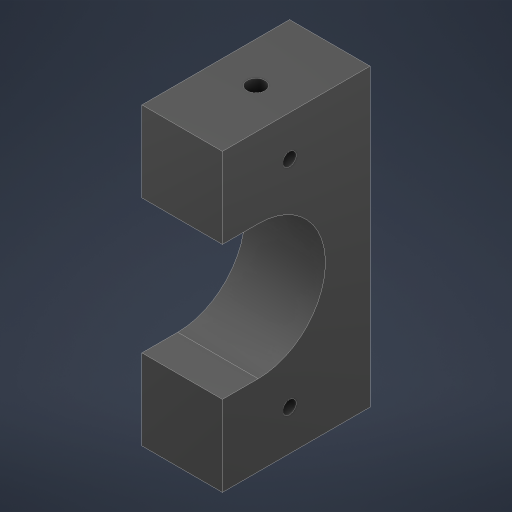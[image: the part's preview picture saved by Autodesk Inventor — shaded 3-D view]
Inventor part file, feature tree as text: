
AUTODESK INVENTOR PART (.ipt)
format: ipt  version: 2024 (Build 280153000, 153)  size: 223,232 bytes
history: native  units: in
note: dims shown in document units (in); Inventor stores cm internally (conversion verified against a paired STEP export)
features: extrude x2, sketch x2, other x1
ambient origin geometry x8: Origin, YZ Plane, XZ Plane, XY Plane, X Axis, Y Axis, Z Axis, Center Point
bodies: Body1 (feature_tree)
feature tree (5):
  other  "Sólido1"
  extrude  "Extrusión1"  Depth=0.3543in
  extrude  "Extrusión2"  Depth=0.1969in TaperAngle=0.0deg
  sketch  "Boceto1"  dims[d0=0.1575in d1=0.3543in]
  sketch  "Boceto2"  dims[d2=0.6496in d3=0.1969in d4=0.0in d5=0.1575in d6=0.3543in d7=0.6496in d8=0.1969in d9=0.0in]
